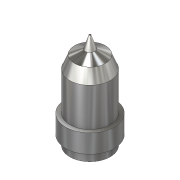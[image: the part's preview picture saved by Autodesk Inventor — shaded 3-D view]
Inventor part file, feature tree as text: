
AUTODESK INVENTOR PART (.ipt)
format: ipt  version: 2019.4 (Build 234330000, 330)  size: 114,688 bytes
history: native  units: mm
features: revolve x1, sketch x1
ambient origin geometry x8: Origin, YZ Plane, XZ Plane, XY Plane, X Axis, Y Axis, Z Axis, Center Point
bodies: Solid1 (feature_tree)
feature tree (2):
  revolve  "Revolution1"  [1 undecoded]
  sketch  "Sketch1"  dims[d0=43.1mm d1=10.125mm d2=4.67mm d3=2.025mm d4=90.0deg d5=9.27mm d6=19.21mm d7=7.73mm d8=39.36mm d9=90.0deg]
note: 1 required parameter value undecoded (feature->parameter linkage not recoverable at this tier; creation-order binding heuristic only, values carry confidence <= 0.55)
